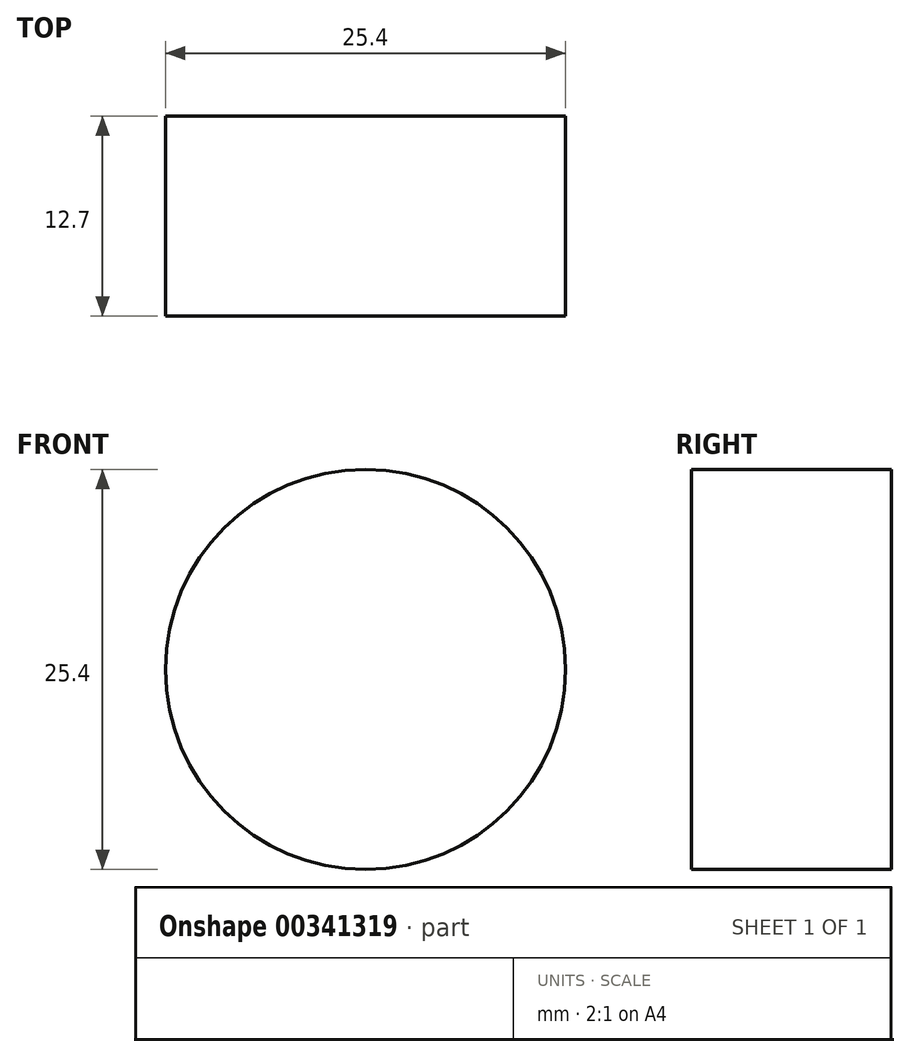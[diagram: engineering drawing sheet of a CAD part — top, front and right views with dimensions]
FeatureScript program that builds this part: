
annotation { "Feature Type Name" : "Feature", "Feature Type Description" : "" }
export const myFeature = defineFeature(function(context is Context, id is Id, definition is map)
    precondition{}
    {
        {
            var Q0;
            Q0=qCreatedBy(makeId("Front.planeOp"),FACE);
            var sketch = newSketch(context, id + "F0", { "sketchPlane" : qUnion([Q0])});
            skCircle(sketch, "E0", {"center": v(0, 0) * mm, "radius": 12.7 * mm});
            skSolve(sketch);
        }
        {
            var Q0;
            Q0 = qSketchRegion(id + "F0", true);
            extrude(context, id + "F1", {"entities" : qUnion([Q0]), "depth" : 12.7 * mm});
        }
    });
